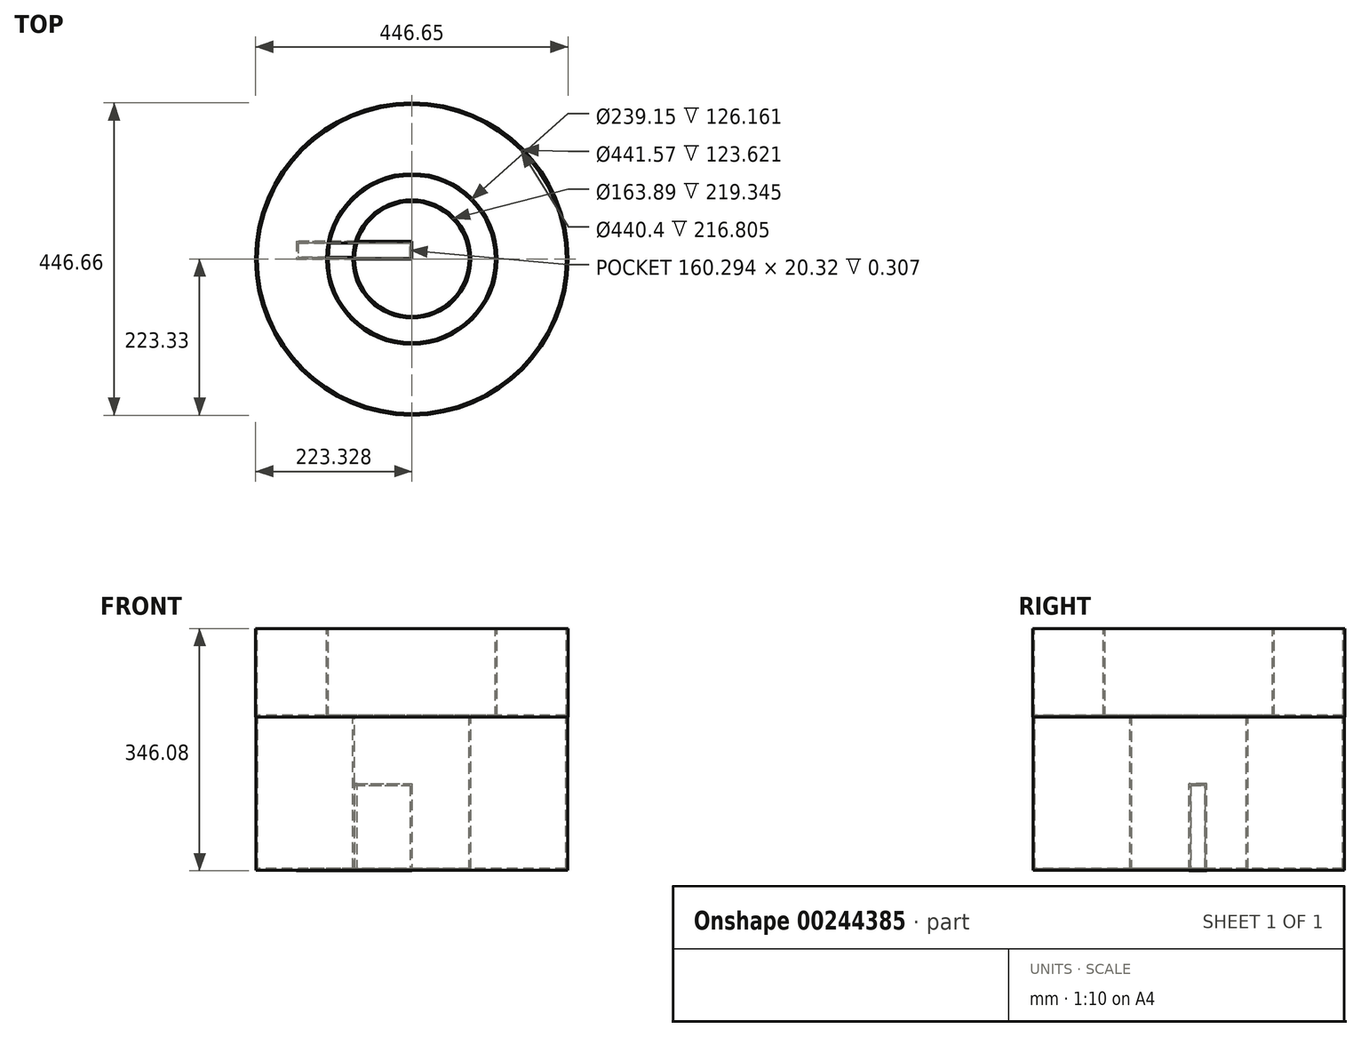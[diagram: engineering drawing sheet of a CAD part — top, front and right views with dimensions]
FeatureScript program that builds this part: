
annotation { "Feature Type Name" : "Feature", "Feature Type Description" : "" }
export const myFeature = defineFeature(function(context is Context, id is Id, definition is map)
    precondition{}
    {
        {
            var Q0;
            Q0=qCreatedBy(makeId("Front.planeOp"),FACE);
            var sketch = newSketch(context, id + "F0", { "sketchPlane" : qUnion([Q0])});
            skLineSegment(sketch, "E0.bottom", {"start": v(-94.14, 59.96) * mm, "end": v(71.24, 59.96) * mm});
            skLineSegment(sketch, "E0.top", {"start": v(-94.14, -64.45) * mm, "end": v(71.24, -64.45) * mm});
            skLineSegment(sketch, "E0.left", {"start": v(-94.14, 59.96) * mm, "end": v(-94.14, -64.45) * mm});
            skLineSegment(sketch, "E0.right", {"start": v(71.24, 59.96) * mm, "end": v(71.24, -64.45) * mm});
            skSolve(sketch);
        }
        {
            var Q0;
            Q0=qSketchRegion(id+"F0",true);
            extrude(context, id + "F1", {"entities" : qUnion([Q0]), "depth" : 25.4 * mm});
        }
        {
            var Q0;
            Q0=qCreatedBy(makeId("Right.planeOp"),FACE);
            var sketch = newSketch(context, id + "F2", { "sketchPlane" : qUnion([Q0])});
            skLineSegment(sketch, "E1.bottom", {"start": v(70.64, 281.63) * mm, "end": v(186.26, 281.63) * mm});
            skLineSegment(sketch, "E1.top", {"start": v(70.64, 155.46) * mm, "end": v(186.26, 155.46) * mm});
            skLineSegment(sketch, "E1.left", {"start": v(70.64, 281.63) * mm, "end": v(70.64, 155.46) * mm});
            skLineSegment(sketch, "E1.right", {"start": v(186.26, 281.63) * mm, "end": v(186.26, 155.46) * mm});
            skLineSegment(sketch, "E2.bottom", {"start": v(15.1, 155.2) * mm, "end": v(185.64, 155.2) * mm});
            skLineSegment(sketch, "E2.top", {"start": v(15.1, -64.15) * mm, "end": v(185.64, -64.15) * mm});
            skLineSegment(sketch, "E2.left", {"start": v(15.1, 155.2) * mm, "end": v(15.1, -64.15) * mm});
            skLineSegment(sketch, "E2.right", {"start": v(185.64, 155.2) * mm, "end": v(185.64, -64.15) * mm});
            skSolve(sketch);
        }
        {
            var Q0;
            Q0=qSketchRegion(id+"F2",true);
            var Q1;
            Q1=makeQuery(id+"F1.opExtrude","CAP_EDGE",EDGE,{"disambiguationData":[OSD([sQuery(id+"F0.wireOp",EDGE,"E0.right")])],"isStart":false});
            revolve(context, id + "F4", {"operationType" : NewBodyOperationType.ADD, "entities" : qUnion([Q0]), "axis" : qUnion([Q1]), "revolveType" : RevolveType.FULL});
        }
        {
            var Q0;
            Q0=makeQuery(id+"F4.opRevolve","SWEPT_FACE",FACE,{"disambiguationData":[OSD([sQuery(id+"F2.wireOp",EDGE,"E1.bottom")])]});
            var Q1;
            Q1=makeQuery(id+"F4.opRevolve","SWEPT_FACE",FACE,{"disambiguationData":[OSD([sQuery(id+"F2.wireOp",EDGE,"E2.bottom")])]});
            shell(context, id + "F3", {"entities" : qUnion([Q0, Q1]), "thickness" : 2.54 * mm});
        }
    });
